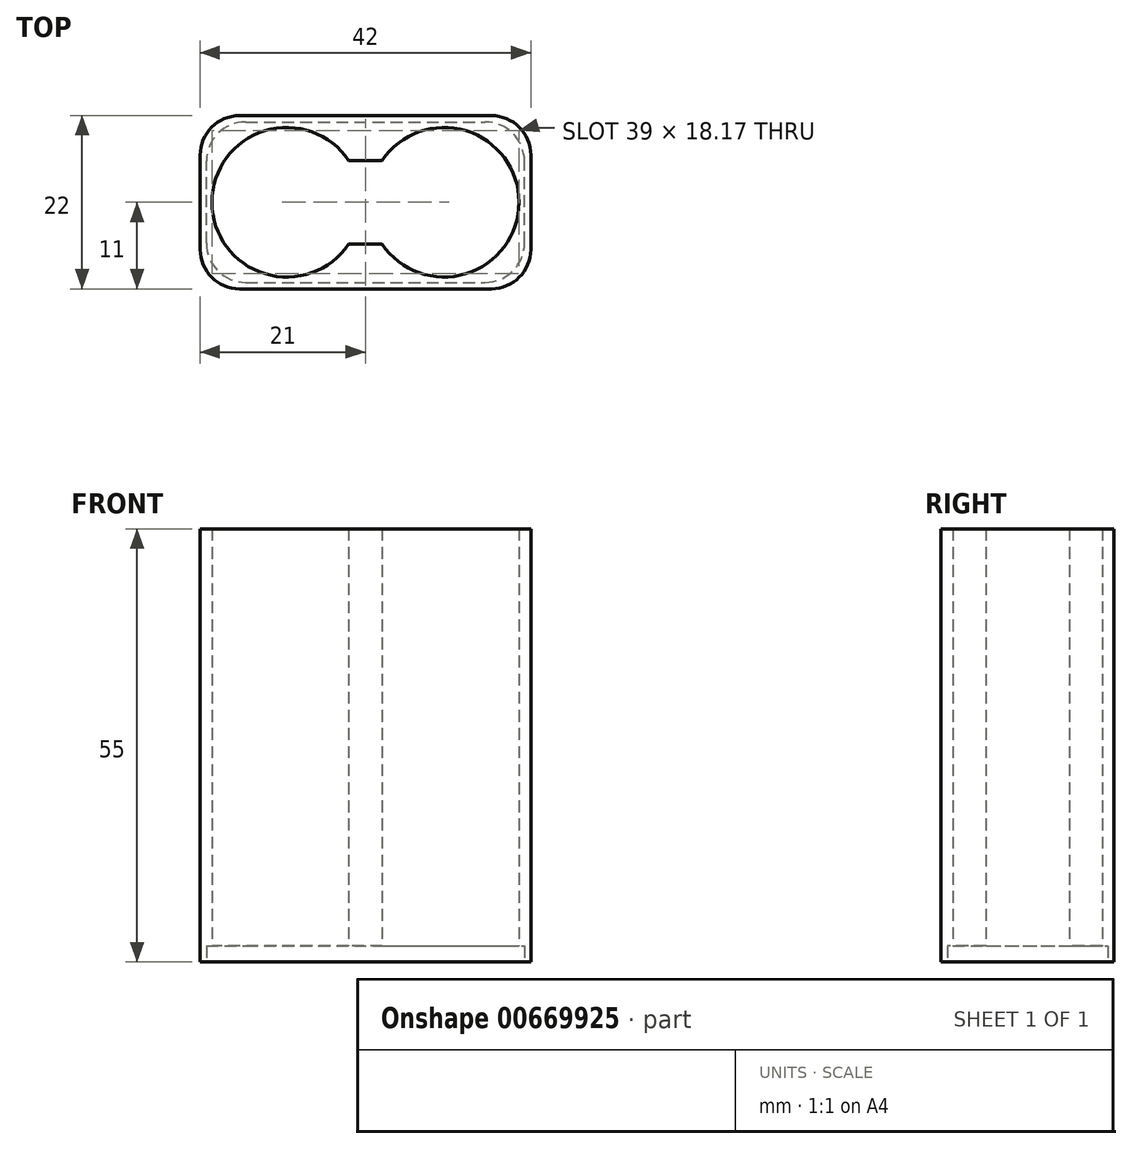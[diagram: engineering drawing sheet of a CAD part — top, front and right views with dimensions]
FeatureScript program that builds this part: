
annotation { "Feature Type Name" : "Feature", "Feature Type Description" : "" }
export const myFeature = defineFeature(function(context is Context, id is Id, definition is map)
    precondition{}
    {
        {
            var Q0;
            Q0=qCreatedBy(makeId("Top.planeOp"),FACE);
            var sketch = newSketch(context, id + "F0", { "sketchPlane" : qUnion([Q0])});
            skLineSegment(sketch, "E0.bottom", {"start": v(-21, 11) * mm, "end": v(21, 11) * mm});
            skLineSegment(sketch, "E0.top", {"start": v(-21, -11) * mm, "end": v(21, -11) * mm});
            skLineSegment(sketch, "E0.left", {"start": v(-21, 11) * mm, "end": v(-21, -11) * mm});
            skLineSegment(sketch, "E0.right", {"start": v(21, 11) * mm, "end": v(21, -11) * mm});
            skCircle(sketch, "E1", {"center": v(-10, 0) * mm, "radius": 9.5 * mm});
            skCircle(sketch, "E2", {"center": v(10, 0) * mm, "radius": 9.5 * mm});
            skLineSegment(sketch, "E3.bottom", {"start": v(-2.12, 5.3) * mm, "end": v(2.12, 5.3) * mm});
            skLineSegment(sketch, "E3.top", {"start": v(-2.12, -5.3) * mm, "end": v(2.12, -5.3) * mm});
            skLineSegment(sketch, "E3.left", {"start": v(-2.12, 5.3) * mm, "end": v(-2.12, -5.3) * mm});
            skLineSegment(sketch, "E3.right", {"start": v(2.12, 5.3) * mm, "end": v(2.12, -5.3) * mm});
            skSolve(sketch);
        }
        {
            var Q0;
            Q0 = qSketchRegion(id + "F0", true);
            extrude(context, id + "F1", {"entities" : qUnion([Q0]), "depth" : 55 * mm, "offsetDistance" : 25 * mm});
        }
        {
            var Q0;
            Q0=makeQuery(id+"F1.opExtrude","CAP_FACE",FACE,{"disambiguationData":[OSD([sQuery(id+"F0.wireOp",EDGE,"E0.bottom"),sQuery(id+"F0.wireOp",EDGE,"E0.top"),sQuery(id+"F0.wireOp",EDGE,"E0.left"),sQuery(id+"F0.wireOp",EDGE,"E0.right"),sQuery(id+"F0.wireOp",EDGE,"E1"),sQuery(id+"F0.wireOp",EDGE,"E2"),sQuery(id+"F0.wireOp",EDGE,"E3.bottom"),sQuery(id+"F0.wireOp",EDGE,"E3.top")])],"isStart":true});
            var sketch = newSketch(context, id + "F2", { "sketchPlane" : qUnion([Q0])});
            skLineSegment(sketch, "E4.bottom", {"start": v(-20.2, 10.2) * mm, "end": v(20.2, 10.2) * mm});
            skLineSegment(sketch, "E4.top", {"start": v(-20.2, -10.2) * mm, "end": v(20.2, -10.2) * mm});
            skLineSegment(sketch, "E4.left", {"start": v(-20.2, 10.2) * mm, "end": v(-20.2, -10.2) * mm});
            skLineSegment(sketch, "E4.right", {"start": v(20.2, 10.2) * mm, "end": v(20.2, -10.2) * mm});
            skSolve(sketch);
        }
        {
            var Q0;
            Q0 = qSketchRegion(id + "F2", true);
            extrude(context, id + "F3", {"entities" : qUnion([Q0]), "operationType" : NewBodyOperationType.REMOVE, "oppositeDirection" : true, "depth" : 2 * mm, "offsetDistance" : 25 * mm});
        }
        {
            var Q0;
            Q0=makeQuery(id+"F3.boolean.opBoolean","COPY",EDGE,{"derivedFrom":makeQuery(id+"F3.opExtrude","SWEPT_EDGE",EDGE,{"disambiguationData":[OSD([sQuery(id+"F2.wireOp",EDGE,"E4.bottom"),sQuery(id+"F2.wireOp",EDGE,"E4.left")])]})});
            var Q1;
            Q1=makeQuery(id+"F3.boolean.opBoolean","COPY",EDGE,{"derivedFrom":makeQuery(id+"F3.opExtrude","SWEPT_EDGE",EDGE,{"disambiguationData":[OSD([sQuery(id+"F2.wireOp",EDGE,"E4.bottom"),sQuery(id+"F2.wireOp",EDGE,"E4.right")])]})});
            var Q2;
            Q2=makeQuery(id+"F3.boolean.opBoolean","COPY",EDGE,{"derivedFrom":makeQuery(id+"F3.opExtrude","SWEPT_EDGE",EDGE,{"disambiguationData":[OSD([sQuery(id+"F2.wireOp",EDGE,"E4.top"),sQuery(id+"F2.wireOp",EDGE,"E4.right")])]})});
            var Q3;
            Q3=makeQuery(id+"F3.boolean.opBoolean","COPY",EDGE,{"derivedFrom":makeQuery(id+"F3.opExtrude","SWEPT_EDGE",EDGE,{"disambiguationData":[OSD([sQuery(id+"F2.wireOp",EDGE,"E4.top"),sQuery(id+"F2.wireOp",EDGE,"E4.left")])]})});
            var Q4;
            Q4=makeQuery(id+"F1.opExtrude","SWEPT_EDGE",EDGE,{"disambiguationData":[OSD([sQuery(id+"F0.wireOp",EDGE,"E0.top"),sQuery(id+"F0.wireOp",EDGE,"E0.right")])]});
            var Q5;
            Q5=makeQuery(id+"F1.opExtrude","SWEPT_EDGE",EDGE,{"disambiguationData":[OSD([sQuery(id+"F0.wireOp",EDGE,"E0.top"),sQuery(id+"F0.wireOp",EDGE,"E0.left")])]});
            var Q6;
            Q6=makeQuery(id+"F1.opExtrude","SWEPT_EDGE",EDGE,{"disambiguationData":[OSD([sQuery(id+"F0.wireOp",EDGE,"E0.bottom"),sQuery(id+"F0.wireOp",EDGE,"E0.right")])]});
            var Q7;
            Q7=makeQuery(id+"F1.opExtrude","SWEPT_EDGE",EDGE,{"disambiguationData":[OSD([sQuery(id+"F0.wireOp",EDGE,"E0.bottom"),sQuery(id+"F0.wireOp",EDGE,"E0.left")])]});
            fillet(context, id + "F4", {"entities" : qUnion([Q0, Q1, Q2, Q3, Q4, Q5, Q6, Q7]), "radius" : 5 * mm, "tangentPropagation" : true, "allowEdgeOverflow" : false});
        }
    });
